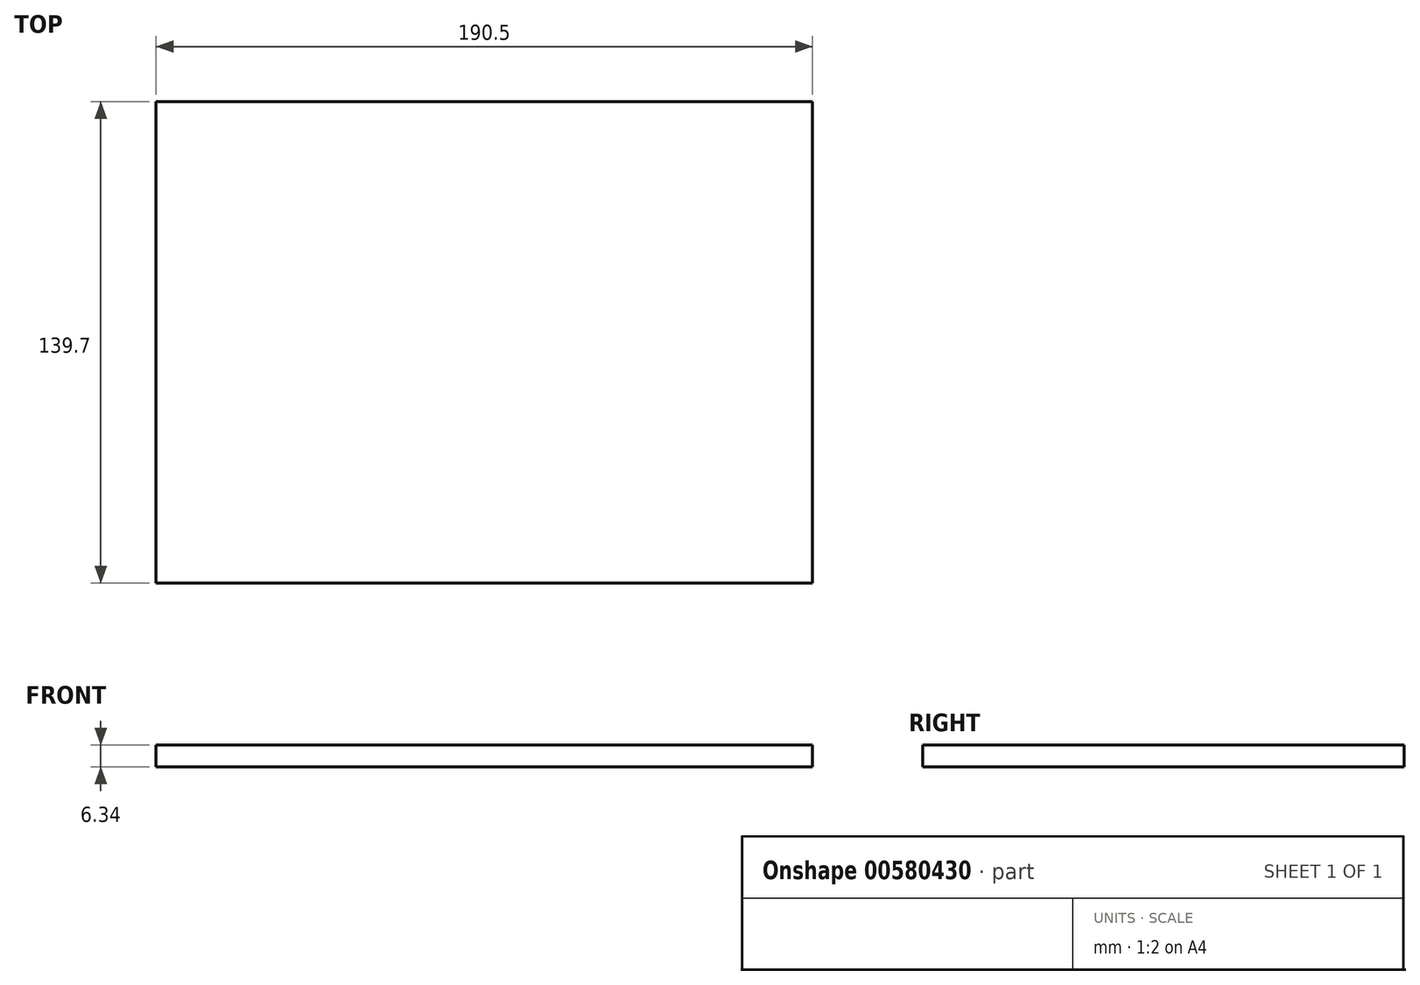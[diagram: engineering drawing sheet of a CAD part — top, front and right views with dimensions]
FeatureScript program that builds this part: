
annotation { "Feature Type Name" : "Feature", "Feature Type Description" : "" }
export const myFeature = defineFeature(function(context is Context, id is Id, definition is map)
    precondition{}
    {
        {
            var Q0;
            Q0=qCreatedBy(makeId("Front.planeOp"),FACE);
            var sketch = newSketch(context, id + "F0", { "sketchPlane" : qUnion([Q0])});
            skLineSegment(sketch, "E0.bottom", {"start": v(95.25, 3.18) * mm, "end": v(-95.25, 3.18) * mm});
            skLineSegment(sketch, "E0.top", {"start": v(95.25, -3.17) * mm, "end": v(-95.25, -3.17) * mm});
            skLineSegment(sketch, "E0.left", {"start": v(95.25, 3.18) * mm, "end": v(95.25, -3.17) * mm});
            skLineSegment(sketch, "E0.right", {"start": v(-95.25, 3.18) * mm, "end": v(-95.25, -3.17) * mm});
            skPoint(sketch, "E0.middle", {"position": v(0, 0) * mm});
            skSolve(sketch);
        }
        {
            var Q0;
            Q0=makeQuery(id+"F0.imprint","IMPRINT",FACE,{"disambiguationData":[TD([[makeQuery(id+"F0.imprint","IMPRINT",EDGE,{"derivedFrom":sQuery(id+"F0.wireOp",EDGE,"E0.bottom")}),1.0]])]});
            extrude(context, id + "F1", {"entities" : qUnion([Q0]), "depth" : 139.7 * mm, "offsetDistance" : 25.4 * mm});
        }
    });
